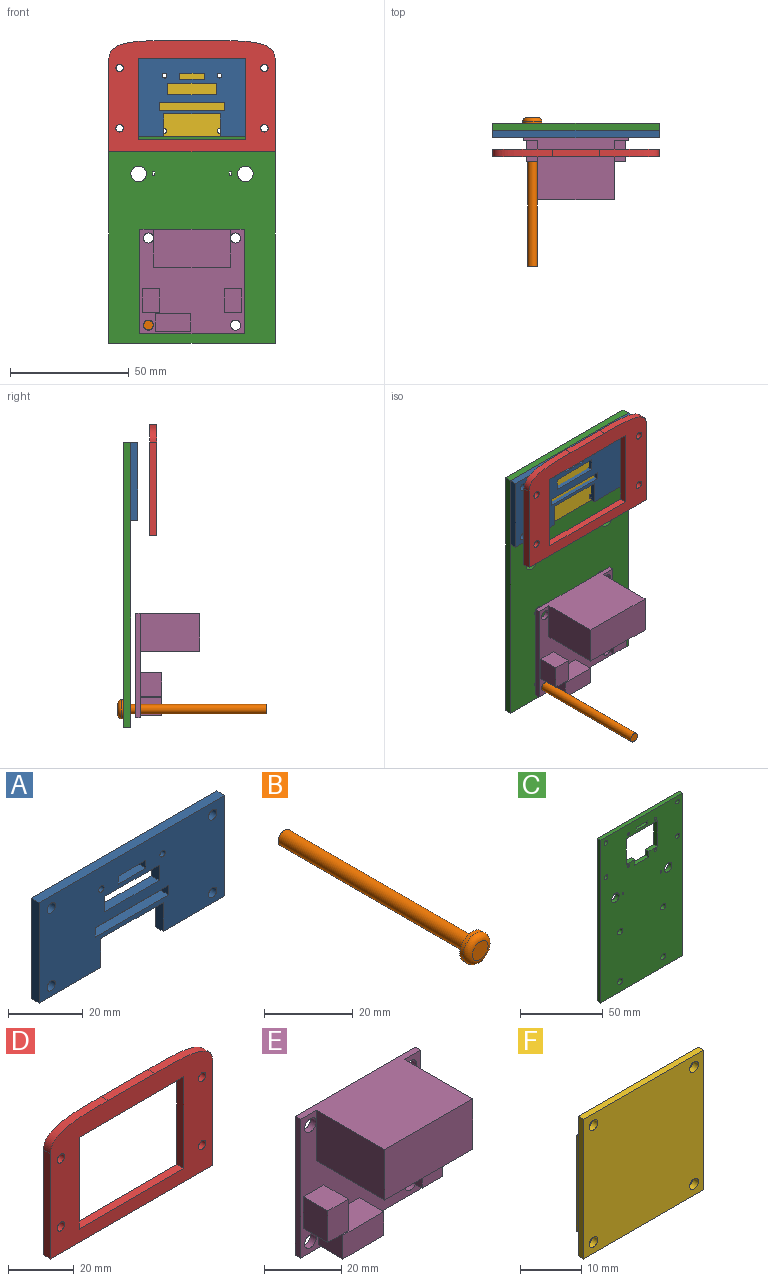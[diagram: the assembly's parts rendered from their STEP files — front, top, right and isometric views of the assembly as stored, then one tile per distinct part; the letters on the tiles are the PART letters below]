
ASSEMBLY  parts=6 mates=5
PART A: 28 faces, bbox 70x3x32.8 mm
  f0: plane 9.45x3mm, normal (1,0,0), area 28.4mm2, adj f1,f19,f26,f27
  f1: plane 23.6x3mm, normal (0,0,-1), area 70.8mm2, adj f0,f2,f26,f27
  f2: plane 9.45x3mm, normal (-1,0,0), area 28.4mm2, adj f1,f3,f26,f27
  f3: plane 23.2x3mm, normal (0,0,-1), area 69.6mm2, adj f2,f4,f26,f27
  f4: plane 32.8x3mm, normal (1,0,0), area 98.4mm2, adj f3,f5,f26,f27
  f5: plane 70x3mm, normal (0,0,1), area 210mm2, adj f4,f6,f26,f27
  f6: plane 32.8x3mm, normal (-1,0,0), area 98.4mm2, adj f5,f19,f26,f27
  f7: plane 20.6x3mm, normal (0,0,1), area 61.8mm2, adj f8,f20,f26,f27
  f8: plane 5x3mm, normal (1,0,0), area 15mm2, adj f7,f9,f26,f27
  f9: plane 20.6x3mm, normal (0,0,-1), area 61.8mm2, adj f8,f20,f26,f27
  f10: plane 3.1x3mm, normal (1,0,0), area 9.3mm2, adj f11,f21,f26,f27
  f11: plane 27.6x3mm, normal (0,0,-1), area 82.8mm2, adj f10,f12,f26,f27
  f12: plane 3.1x3mm, normal (-1,0,0), area 9.3mm2, adj f11,f21,f26,f27
  f13: plane 10.4x3mm, normal (0,0,1), area 31.2mm2, adj f14,f22,f26,f27
  f14: plane 3x2.6mm, normal (1,0,0), area 7.8mm2, adj f13,f15,f26,f27
  f15: plane 10.4x3mm, normal (0,0,-1), area 31.2mm2, adj f14,f22,f26,f27
  f16: cylinder r=1.57mm len=3.15mm, axis (0,1,0), area 29.7mm2, adj f26,f27
  f17: cylinder r=1.57mm len=3.15mm, axis (0,1,0), area 29.7mm2, adj f26,f27
  f18: cylinder r=1.57mm len=3.15mm, axis (0,1,0), area 29.7mm2, adj f26,f27
  f19: plane 23.2x3mm, normal (0,0,-1), area 69.6mm2, adj f0,f6,f26,f27
  f20: plane 5x3mm, normal (-1,0,0), area 15mm2, adj f7,f9,f26,f27
  f21: plane 27.6x3mm, normal (0,0,1), area 82.8mm2, adj f10,f12,f26,f27
  f22: plane 3x2.6mm, normal (-1,0,0), area 7.8mm2, adj f13,f15,f26,f27
  f23: cylinder r=1mm len=3mm, axis (0,1,0), area 18.8mm2, adj f26,f27
  f24: cylinder r=1mm len=3mm, axis (0,1,0), area 18.8mm2, adj f26,f27
  f25: cylinder r=1.57mm len=3.15mm, axis (0,1,0), area 29.7mm2, adj f26,f27
  f26: plane 70x32.8mm, normal (0,-1,0), area 1819.9mm2, adj f0,f1,f2,f3,f4,f5,f6,f7
  f27: plane 70x32.8mm, normal (0,1,0), area 1819.9mm2, adj f0,f1,f2,f3,f4,f5,f6,f7
PART B: 6 faces, bbox 8.7x62.5x8.7 mm
  f0: plane 8x8mm, normal (0,1,0), area 37.7mm2, adj f1,f5
  f1: cylinder r=4mm len=8mm, axis (0,1,0), area 25.1mm2, adj f0,f2
  f2: torus R=2.5mm, axis (0,1,0), area 51.1mm2, adj f1,f3
  f3: plane 5x5mm, normal (0,-1,0), area 19.6mm2, adj f2
  f4: plane 4x4mm, normal (0,1,0), area 12.6mm2, adj f5
  f5: cylinder r=2mm len=60mm, axis (0,1,0), area 754mm2, adj f0,f4
PART C: 40 faces, bbox 70x3x120 mm
  f0: plane 120x70mm, normal (0,-1,0), area 7652.2mm2, adj f2,f3,f4,f5,f6,f7,f8,f9
  f1: plane 120x70mm, normal (0,1,0), area 7652.2mm2, adj f2,f3,f4,f5,f6,f7,f8,f9
  f2: plane 120x3mm, normal (1,0,0), area 360mm2, adj f0,f1,f3,f5
  f3: plane 70x3mm, normal (0,0,1), area 210mm2, adj f0,f1,f2,f4
  f4: plane 120x3mm, normal (-1,0,0), area 360mm2, adj f0,f1,f3,f5
  f5: plane 70x3mm, normal (0,0,-1), area 210mm2, adj f0,f1,f2,f4
  f6: plane 7.3x3mm, normal (0,0,1), area 21.9mm2, adj f0,f1,f7,f13
  f7: plane 19.11x3mm, normal (-1,0,0), area 57.3mm2, adj f0,f1,f6,f8
  f8: plane 26.6x3mm, normal (0,0,-1), area 79.8mm2, adj f0,f1,f7,f9
  f9: plane 19.11x3mm, normal (1,0,0), area 57.3mm2, adj f0,f1,f8,f10
  f10: plane 7.3x3mm, normal (0,0,1), area 21.9mm2, adj f0,f1,f9,f11
  f11: plane 4.19x3mm, normal (1,0,0), area 12.6mm2, adj f0,f1,f10,f12
  f12: plane 12x3mm, normal (0,0,1), area 36mm2, adj f0,f1,f11,f13
  f13: plane 4.19x3mm, normal (-1,0,0), area 12.6mm2, adj f0,f1,f6,f12
  f14: cylinder r=1mm len=3mm, axis (0,-1,0), area 18.8mm2, adj f0,f1
  f15: cylinder r=1mm len=3mm, axis (0,-1,0), area 18.8mm2, adj f0,f1
  f16: cylinder r=1mm len=3mm, axis (0,-1,0), area 18.8mm2, adj f0,f1
  f17: cylinder r=1mm len=3mm, axis (0,-1,0), area 18.8mm2, adj f0,f1
  f18: plane 3x2mm, normal (-1,0,0), area 6mm2, adj f0,f1,f19,f21
  f19: plane 9.5x3mm, normal (0,0,-1), area 28.5mm2, adj f0,f1,f18,f20
  f20: plane 3x2mm, normal (1,0,0), area 6mm2, adj f0,f1,f19,f21
  f21: plane 9.5x3mm, normal (0,0,1), area 28.5mm2, adj f0,f1,f18,f20
  f22: plane 3x1.65mm, normal (-1,0,0), area 5mm2, adj f0,f1,f23,f25
  f23: plane 3x1mm, normal (0,0,-1), area 3mm2, adj f0,f1,f22,f24
  f24: plane 3x1.65mm, normal (1,0,0), area 5mm2, adj f0,f1,f23,f25
  f25: plane 3x1mm, normal (0,0,1), area 3mm2, adj f0,f1,f22,f24
  f26: plane 3x1.65mm, normal (1,0,0), area 5mm2, adj f0,f1,f27,f29
  f27: plane 3x1mm, normal (0,0,1), area 3mm2, adj f0,f1,f26,f28
  f28: plane 3x1.65mm, normal (-1,0,0), area 5mm2, adj f0,f1,f27,f29
  f29: plane 3x1mm, normal (0,0,-1), area 3mm2, adj f0,f1,f26,f28
  f30: cylinder r=3.25mm len=6.5mm, axis (0,1,0), area 61.3mm2, adj f0,f1
  f31: cylinder r=3.25mm len=6.5mm, axis (0,1,0), area 61.3mm2, adj f0,f1
  f32: cylinder r=2.12mm len=4.25mm, axis (0,-1,0), area 40.1mm2, adj f0,f1
  f33: cylinder r=2.12mm len=4.25mm, axis (0,-1,0), area 40.1mm2, adj f0,f1
  f34: cylinder r=2.12mm len=4.25mm, axis (0,-1,0), area 40.1mm2, adj f0,f1
  f35: cylinder r=2.12mm len=4.25mm, axis (0,-1,0), area 40.1mm2, adj f0,f1
  f36: cylinder r=1.57mm len=3.15mm, axis (0,-1,0), area 29.7mm2, adj f0,f1
  f37: cylinder r=1.57mm len=3.15mm, axis (0,-1,0), area 29.7mm2, adj f0,f1
  f38: cylinder r=1.57mm len=3.15mm, axis (0,-1,0), area 29.7mm2, adj f0,f1
  f39: cylinder r=1.57mm len=3.15mm, axis (0,-1,0), area 29.7mm2, adj f0,f1
PART D: 16 faces, bbox 70x3x46.8 mm
  f0: plane 39.25x3mm, normal (1,0,0), area 117.7mm2, adj f1,f11,f14,f15
  f1: extruded ~25x7.5mm, area 85.2mm2, adj f0,f2,f14,f15
  f2: plane 20x3mm, normal (0,0,1), area 60mm2, adj f1,f3,f14,f15
  f3: extruded ~25x7.5mm, area 85.2mm2, adj f2,f4,f14,f15
  f4: plane 39.25x3mm, normal (-1,0,0), area 117.7mm2, adj f3,f11,f14,f15
  f5: plane 34.25x3mm, normal (-1,0,0), area 102.8mm2, adj f6,f12,f14,f15
  f6: plane 45.25x3mm, normal (0,0,1), area 135.7mm2, adj f5,f7,f14,f15
  f7: plane 34.25x3mm, normal (1,0,0), area 102.8mm2, adj f6,f12,f14,f15
  f8: cylinder r=1.57mm len=3.15mm, axis (0,1,0), area 29.7mm2, adj f14,f15
  f9: cylinder r=1.57mm len=3.15mm, axis (0,1,0), area 29.7mm2, adj f14,f15
  f10: cylinder r=1.57mm len=3.15mm, axis (0,1,0), area 29.7mm2, adj f14,f15
  f11: plane 70x3mm, normal (0,0,-1), area 210mm2, adj f0,f4,f14,f15
  f12: plane 45.25x3mm, normal (0,0,-1), area 135.7mm2, adj f5,f7,f14,f15
  f13: cylinder r=1.57mm len=3.15mm, axis (0,1,0), area 29.7mm2, adj f14,f15
  f14: plane 70x46.75mm, normal (0,-1,0), area 1644.9mm2, adj f0,f1,f2,f3,f4,f5,f6,f7
  f15: plane 70x46.75mm, normal (0,1,0), area 1644.9mm2, adj f0,f1,f2,f3,f4,f5,f6,f7
PART E: 29 faces, bbox 44x27x44 mm
  f0: plane 44x44mm, normal (0,-1,0), area 1100.8mm2, adj f1,f2,f3,f4,f6,f7,f8,f9
  f1: plane 44x2mm, normal (-1,0,0), area 88mm2, adj f0,f2,f4,f5
  f2: plane 44x2mm, normal (0,0,-1), area 88mm2, adj f0,f1,f3,f5
  f3: plane 44x2mm, normal (1,0,0), area 88mm2, adj f0,f2,f4,f5
  f4: plane 44x27mm, normal (0,0,1), area 894.2mm2, adj f0,f1,f3,f5,f10,f12,f13
  f5: plane 44x44mm, normal (0,1,0), area 1879.3mm2, adj f1,f2,f3,f4,f6,f7,f8,f9
  f6: cylinder r=2.12mm len=4.25mm, axis (0,-1,0), area 26.7mm2, adj f0,f5
  f7: cylinder r=2.12mm len=4.25mm, axis (0,-1,0), area 26.7mm2, adj f0,f5
  f8: cylinder r=2.12mm len=4.25mm, axis (0,-1,0), area 26.7mm2, adj f0,f5
  f9: cylinder r=2.12mm len=4.25mm, axis (0,-1,0), area 26.7mm2, adj f0,f5
  f10: plane 25x16mm, normal (-1,0,0), area 400mm2, adj f0,f4,f11,f13
  f11: plane 32.25x25mm, normal (0,0,-1), area 806.3mm2, adj f0,f10,f12,f13
  f12: plane 25x16mm, normal (1,0,0), area 400mm2, adj f0,f4,f11,f13
  f13: plane 32.25x16mm, normal (0,-1,0), area 516mm2, adj f4,f10,f11,f12
  f14: plane 10x9mm, normal (1,0,0), area 90mm2, adj f0,f15,f17,f18
  f15: plane 9x7.5mm, normal (0,0,1), area 67.5mm2, adj f0,f14,f16,f18
  f16: plane 10x9mm, normal (-1,0,0), area 90mm2, adj f0,f15,f17,f18
  f17: plane 9x7.5mm, normal (0,0,-1), area 67.5mm2, adj f0,f14,f16,f18
  f18: plane 10x7.5mm, normal (0,-1,0), area 75mm2, adj f14,f15,f16,f17
  f19: plane 9x7.5mm, normal (0,0,1), area 67.5mm2, adj f0,f20,f22,f23
  f20: plane 10x9mm, normal (-1,0,0), area 90mm2, adj f0,f19,f21,f23
  f21: plane 9x7.5mm, normal (0,0,-1), area 67.5mm2, adj f0,f20,f22,f23
  f22: plane 10x9mm, normal (1,0,0), area 90mm2, adj f0,f19,f21,f23
  f23: plane 10x7.5mm, normal (0,-1,0), area 75mm2, adj f19,f20,f21,f22
  f24: plane 9x7.5mm, normal (1,0,0), area 67.5mm2, adj f0,f25,f27,f28
  f25: plane 15x9mm, normal (0,0,1), area 135mm2, adj f0,f24,f26,f28
  f26: plane 9x7.5mm, normal (-1,0,0), area 67.5mm2, adj f0,f25,f27,f28
  f27: plane 15x9mm, normal (0,0,-1), area 135mm2, adj f0,f24,f26,f28
  f28: plane 15x7.5mm, normal (0,-1,0), area 112.5mm2, adj f24,f25,f26,f27
PART F: 18 faces, bbox 27.6x2.3x27.8 mm
  f0: plane 7.3x1mm, normal (0,0,-1), area 7.3mm2, adj f1,f7,f8,f17
  f1: plane 19.11x1mm, normal (1,0,0), area 19.1mm2, adj f0,f2,f8,f17
  f2: plane 26.6x1mm, normal (0,0,1), area 26.6mm2, adj f1,f3,f8,f17
  f3: plane 19.11x1mm, normal (-1,0,0), area 19.1mm2, adj f2,f4,f8,f17
  f4: plane 7.3x1mm, normal (0,0,-1), area 7.3mm2, adj f3,f5,f8,f17
  f5: plane 4.19x1mm, normal (-1,0,0), area 4.2mm2, adj f4,f6,f8,f17
  f6: plane 27.6x2.25mm, normal (0,0,-1), area 46.5mm2, adj f5,f7,f8,f9,f14,f16,f17
  f7: plane 4.19x1mm, normal (1,0,0), area 4.2mm2, adj f0,f6,f8,f17
  f8: plane 26.6x23.3mm, normal (0,1,0), area 558.6mm2, adj f0,f1,f2,f3,f4,f5,f6,f7
  f9: plane 27.8x1.25mm, normal (1,0,0), area 34.8mm2, adj f6,f10,f16,f17
  f10: plane 27.6x1.25mm, normal (0,0,1), area 34.5mm2, adj f9,f14,f16,f17
  f11: cylinder r=1mm len=2mm, axis (0,1,0), area 7.9mm2, adj f16,f17
  f12: cylinder r=1mm len=2mm, axis (0,1,0), area 7.9mm2, adj f16,f17
  f13: cylinder r=1mm len=2mm, axis (0,1,0), area 7.9mm2, adj f16,f17
  f14: plane 27.8x1.25mm, normal (-1,0,0), area 34.8mm2, adj f6,f10,f16,f17
  f15: cylinder r=1mm len=2mm, axis (0,1,0), area 7.9mm2, adj f16,f17
  f16: plane 27.8x27.6mm, normal (0,-1,0), area 754.7mm2, adj f6,f9,f10,f11,f12,f13,f14,f15
  f17: plane 27.8x27.6mm, normal (0,1,0), area 196.1mm2, adj f0,f1,f2,f3,f4,f5,f6,f7
PLACE A t=(0,1.25,0)mm
PLACE B rot(axis=(1,0,0),180deg) t=(-36.75,-3,-104.75)mm
PLACE C at identity fixed
PLACE D t=(0,-12.5,0)mm
PLACE E t=(0,-4,0)mm
PLACE F at identity
MATE fastened B.f1 <-> C.f35  axis (0,-1,0) through (-18.38,0,-52.38)mm
MATE fastened D.f10 <-> A.f16  axis (0,1,0) through (30.48,-11,56)mm
MATE fastened C.f0 <-> F.f17  axis (0,-1,0) through (0,-3,50.5)mm
MATE fastened A.f27 <-> C.f0  axis (0,1,0) through (0,-3,60)mm
MATE fastened C.f32 <-> E.f6  axis (0,-1,0) through (-18.37,-3,-15.62)mm
